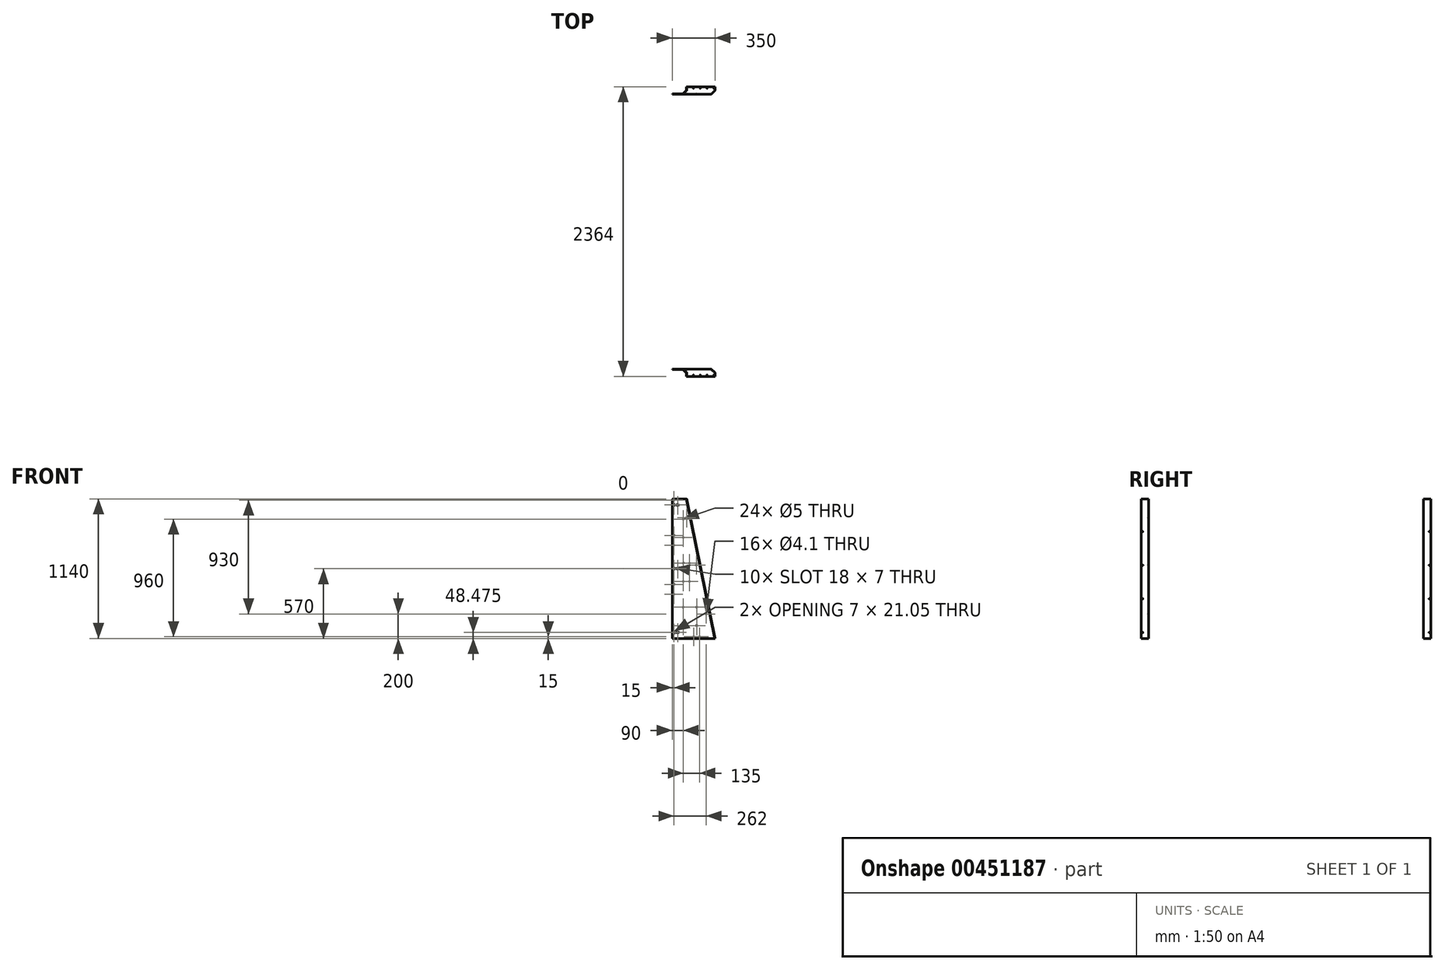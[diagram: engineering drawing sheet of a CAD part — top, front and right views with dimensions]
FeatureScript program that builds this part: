
annotation { "Feature Type Name" : "Feature", "Feature Type Description" : "" }
export const myFeature = defineFeature(function(context is Context, id is Id, definition is map)
    precondition{}
    {
        {
            var Q0;
            Q0=qCreatedBy(makeId("Front.planeOp"),FACE);
            var sketch = newSketch(context, id + "F0", { "sketchPlane" : qUnion([Q0])});
            skLineSegment(sketch, "E0", {"start": v(0, 0) * mm, "end": v(0, 1140) * mm});
            skLineSegment(sketch, "E1", {"start": v(0, 1140) * mm, "end": v(120, 1140) * mm});
            skLineSegment(sketch, "E2", {"start": v(120, 1140) * mm, "end": v(350, 0) * mm});
            skLineSegment(sketch, "E3", {"start": v(350, 0) * mm, "end": v(0, 0) * mm});
            skSolve(sketch);
        }
        {
            var Q0;
            Q0 = qSketchRegion(id + "F0", true);
            extrude(context, id + "F1", {"entities" : qUnion([Q0]), "oppositeDirection" : true, "depth" : 60 * mm, "offsetDistance" : 25 * mm});
        }
        {
            var Q0;
            Q0=makeQuery(id+"F1.opExtrude","SWEPT_FACE",FACE,{"disambiguationData":[OSD([sQuery(id+"F0.wireOp",EDGE,"E1")])]});
            var Q1;
            Q1=makeQuery(id+"F1.opExtrude","SWEPT_FACE",FACE,{"disambiguationData":[OSD([sQuery(id+"F0.wireOp",EDGE,"E0")])]});
            var Q2;
            Q2=makeQuery(id+"F1.opExtrude","CAP_FACE",FACE,{"disambiguationData":[OSD([sQuery(id+"F0.wireOp",EDGE,"E0"),sQuery(id+"F0.wireOp",EDGE,"E1"),sQuery(id+"F0.wireOp",EDGE,"E2"),sQuery(id+"F0.wireOp",EDGE,"E3")])],"isStart":false});
            var Q3;
            Q3=makeQuery(id+"F1.opExtrude","SWEPT_FACE",FACE,{"disambiguationData":[OSD([sQuery(id+"F0.wireOp",EDGE,"E3")])]});
            shell(context, id + "F2", {"entities" : qUnion([Q0, Q1, Q2, Q3]), "thickness" : 3 * mm});
        }
        {
            var Q0;
            Q0=makeQuery(id+"F1.opExtrude","CAP_EDGE",EDGE,{"disambiguationData":[OSD([sQuery(id+"F0.wireOp",EDGE,"E2")])],"isStart":true});
            var Q1;
            {var subQ0=sQuery(id+"F0.wireOp",EDGE,"E2");Q1=makeQuery(id+"F2.opShell","OFFSET_EDGE",EDGE,{"disambiguationData":[OSD([subQ0]),TDD([makeQuery(id+"F1.opExtrude","CAP_EDGE",EDGE,{"disambiguationData":[OSD([subQ0])],"isStart":true})])]});}
            chamfer(context, id + "F3", {"entities" : qUnion([Q0, Q1]), "width" : 30 * mm, "tangentPropagation" : true});
        }
        {
            var Q0;
            {var subQ0=sQuery(id+"F0.wireOp",EDGE,"E2");Q0=makeQuery(id+"F3.opChamfer","BLEND_EDGE",EDGE,{"blendedFrom":[makeQuery(id+"F1.opExtrude","CAP_EDGE",EDGE,{"disambiguationData":[OSD([subQ0])],"isStart":true}),makeQuery(id+"F1.opExtrude","CAP_FACE",FACE,{"disambiguationData":[OSD([sQuery(id+"F0.wireOp",EDGE,"E0"),sQuery(id+"F0.wireOp",EDGE,"E1"),subQ0,sQuery(id+"F0.wireOp",EDGE,"E3")])],"isStart":true})],"blendedInto":[makeQuery(id+"F1.opExtrude","CAP_FACE",FACE,{"disambiguationData":[OSD([sQuery(id+"F0.wireOp",EDGE,"E0"),sQuery(id+"F0.wireOp",EDGE,"E1"),subQ0,sQuery(id+"F0.wireOp",EDGE,"E3")])],"isStart":true})]});}
            var Q1;
            {var subQ0=sQuery(id+"F0.wireOp",EDGE,"E2");Q1=makeQuery(id+"F3.opChamfer","BLEND_EDGE",EDGE,{"blendedFrom":[makeQuery(id+"F2.opShell","OFFSET_EDGE",EDGE,{"disambiguationData":[OSD([subQ0]),TDD([makeQuery(id+"F1.opExtrude","CAP_EDGE",EDGE,{"disambiguationData":[OSD([subQ0])],"isStart":true})])]}),makeQuery(id+"F2.opShell","OFFSET_FACE",FACE,{"disambiguationData":[OSD([sQuery(id+"F0.wireOp",EDGE,"E0"),sQuery(id+"F0.wireOp",EDGE,"E1"),subQ0,sQuery(id+"F0.wireOp",EDGE,"E3")])]})],"blendedInto":[makeQuery(id+"F2.opShell","OFFSET_FACE",FACE,{"disambiguationData":[OSD([sQuery(id+"F0.wireOp",EDGE,"E0"),sQuery(id+"F0.wireOp",EDGE,"E1"),subQ0,sQuery(id+"F0.wireOp",EDGE,"E3")])]})]});}
            var Q2;
            {var subQ0=sQuery(id+"F0.wireOp",EDGE,"E2");Q2=makeQuery(id+"F3.opChamfer","BLEND_EDGE",EDGE,{"blendedFrom":[makeQuery(id+"F1.opExtrude","CAP_EDGE",EDGE,{"disambiguationData":[OSD([subQ0])],"isStart":true}),makeQuery(id+"F1.opExtrude","SWEPT_FACE",FACE,{"disambiguationData":[OSD([subQ0])]})],"blendedInto":[makeQuery(id+"F1.opExtrude","SWEPT_FACE",FACE,{"disambiguationData":[OSD([subQ0])]})]});}
            var Q3;
            {var subQ0=sQuery(id+"F0.wireOp",EDGE,"E2");Q3=makeQuery(id+"F3.opChamfer","BLEND_EDGE",EDGE,{"blendedFrom":[makeQuery(id+"F2.opShell","OFFSET_EDGE",EDGE,{"disambiguationData":[OSD([subQ0]),TDD([makeQuery(id+"F1.opExtrude","CAP_EDGE",EDGE,{"disambiguationData":[OSD([subQ0])],"isStart":true})])]}),makeQuery(id+"F2.opShell","OFFSET_FACE",FACE,{"disambiguationData":[OSD([subQ0])]})],"blendedInto":[makeQuery(id+"F2.opShell","OFFSET_FACE",FACE,{"disambiguationData":[OSD([subQ0])]})]});}
            fillet(context, id + "F4", {"entities" : qUnion([Q0, Q1, Q2, Q3]), "radius" : 10 * mm, "tangentPropagation" : true, "allowEdgeOverflow" : false});
        }
        {
            var Q0;
            Q0=makeQuery(id+"F1.opExtrude","SWEPT_FACE",FACE,{"disambiguationData":[OSD([sQuery(id+"F0.wireOp",EDGE,"E2")])]});
            var sketch = newSketch(context, id + "F5", { "sketchPlane" : qUnion([Q0])});
            skPoint(sketch, "E4", {"position": v(48, -19.22) * mm});
            skPoint(sketch, "E5.0.1.0", {"position": v(48, 260.78) * mm});
            skPoint(sketch, "E5.0.2.0", {"position": v(48, 540.78) * mm});
            skPoint(sketch, "E5.0.3.0", {"position": v(48, 820.78) * mm});
            skPoint(sketch, "E5.0.4.0", {"position": v(48, 1100.78) * mm});
            skLineSegment(sketch, "E5.direction1", {"start": v(48, -19.22) * mm, "end": v(73, -19.22) * mm, "construction": true});
            skLineSegment(sketch, "E5.direction2", {"start": v(48, -19.22) * mm, "end": v(48, 260.78) * mm, "construction": true});
            skSolve(sketch);
        }
        {
            var Q0;
            Q0=makeQuery(id+"F1.opExtrude","CAP_FACE",FACE,{"disambiguationData":[OSD([sQuery(id+"F0.wireOp",EDGE,"E0"),sQuery(id+"F0.wireOp",EDGE,"E1"),sQuery(id+"F0.wireOp",EDGE,"E2"),sQuery(id+"F0.wireOp",EDGE,"E3")])],"isStart":true});
            var sketch = newSketch(context, id + "F6", { "sketchPlane" : qUnion([Q0])});
            skCircle(sketch, "E6", {"center": v(90, 105) * mm, "radius": 2.5 * mm});
            skCircle(sketch, "E7", {"center": v(200, 105) * mm, "radius": 2.5 * mm});
            skCircle(sketch, "E8", {"center": v(200, 255) * mm, "radius": 2.5 * mm});
            skCircle(sketch, "E9", {"center": v(90, 255) * mm, "radius": 2.5 * mm});
            skCircle(sketch, "E10", {"center": v(90, 465) * mm, "radius": 2.5 * mm});
            skCircle(sketch, "E11", {"center": v(90, 615) * mm, "radius": 2.5 * mm});
            skCircle(sketch, "E12", {"center": v(140, 465) * mm, "radius": 2.5 * mm});
            skCircle(sketch, "E13", {"center": v(140, 615) * mm, "radius": 2.5 * mm});
            skCircle(sketch, "E14", {"center": v(90, 825) * mm, "radius": 2.5 * mm});
            skCircle(sketch, "E15", {"center": v(90, 975) * mm, "radius": 2.5 * mm});
            skCircle(sketch, "E16", {"center": v(225, 15) * mm, "radius": 2.5 * mm});
            skCircle(sketch, "E17", {"center": v(175, 15) * mm, "radius": 2.5 * mm});
            skSolve(sketch);
        }
        {
            var Q0;
            Q0 = qSketchRegion(id + "F6", true);
            extrude(context, id + "F7", {"entities" : qUnion([Q0]), "operationType" : NewBodyOperationType.REMOVE, "oppositeDirection" : true, "depth" : 25 * mm, "offsetDistance" : 25 * mm});
        }
        {
            var Q0;
            Q0=sQuery(id+"F5.wireOp",VERTEX,"E4");
            var Q1;
            Q1=sQuery(id+"F5.wireOp",VERTEX,"E5.direction2.end");
            var Q2;
            Q2=sQuery(id+"F5.wireOp",VERTEX,"E5.0.2.0");
            var Q3;
            Q3=sQuery(id+"F5.wireOp",VERTEX,"E5.0.3.0");
            var Q4;
            Q4=sQuery(id+"F5.wireOp",VERTEX,"E5.0.4.0");
            var Q5;
            Q5=makeQuery(id+"F1.opExtrude","SWEPT_BODY",BODY,{"disambiguationData":[OSD([sQuery(id+"F0.wireOp",EDGE,"E0"),sQuery(id+"F0.wireOp",EDGE,"E1"),sQuery(id+"F0.wireOp",EDGE,"E2"),sQuery(id+"F0.wireOp",EDGE,"E3")])]});
            hole(context, id + "F8", {"style" : HoleStyle.SIMPLE, "endStyle" : HoleEndStyle.BLIND, "holeDiameter" : 4.1 * mm, "majorDiameter" : 5 * mm, "holeDepth" : 5 * mm, "tappedDepth" : 12 * mm, "tapClearance" : 3, "locations" : qUnion([Q0, Q1, Q2, Q3, Q4]), "scope" : qUnion([Q5])});
        }
        {
            var Q0;
            Q0=makeQuery(id+"F1.opExtrude","CAP_FACE",FACE,{"disambiguationData":[OSD([sQuery(id+"F0.wireOp",EDGE,"E0"),sQuery(id+"F0.wireOp",EDGE,"E1"),sQuery(id+"F0.wireOp",EDGE,"E2"),sQuery(id+"F0.wireOp",EDGE,"E3")])],"isStart":true});
            var sketch = newSketch(context, id + "F9", { "sketchPlane" : qUnion([Q0])});
            skLineSegment(sketch, "E18.bottom", {"start": v(18.5, 44.5) * mm, "end": v(11.5, 44.5) * mm, "construction": true});
            skLineSegment(sketch, "E18.top", {"start": v(18.5, 55.5) * mm, "end": v(11.5, 55.5) * mm, "construction": true});
            skLineSegment(sketch, "E18.left", {"start": v(18.5, 44.5) * mm, "end": v(18.5, 55.5) * mm});
            skLineSegment(sketch, "E18.right", {"start": v(11.5, 44.5) * mm, "end": v(11.5, 55.5) * mm});
            skPoint(sketch, "E18.middle", {"position": v(15, 50) * mm});
            skArc(sketch, "E19", {"start": v(18.5, 55.5) * mm, "mid": v(15, 59) * mm, "end": v(11.5, 55.5) * mm});
            skArc(sketch, "E20", {"start": v(11.5, 44.5) * mm, "mid": v(15, 41) * mm, "end": v(18.5, 44.5) * mm});
            skLineSegment(sketch, "E21", {"start": v(30, 91.9) * mm, "end": v(30, -40.7) * mm, "construction": true});
            skPoint(sketch, "E22.MirrorP", {"position": v(45, 50) * mm});
            skArc(sketch, "E23.MirrorCS", {"start": v(48.5, 44.5) * mm, "mid": v(45, 41) * mm, "end": v(41.5, 44.5) * mm});
            skLineSegment(sketch, "E24.MirrorCS", {"start": v(41.5, 44.5) * mm, "end": v(48.5, 44.5) * mm, "construction": true});
            skLineSegment(sketch, "E25.MirrorCS", {"start": v(41.5, 55.5) * mm, "end": v(48.5, 55.5) * mm, "construction": true});
            skLineSegment(sketch, "E26.MirrorCS", {"start": v(41.5, 44.5) * mm, "end": v(41.5, 55.5) * mm});
            skLineSegment(sketch, "E27.MirrorCS", {"start": v(48.5, 44.5) * mm, "end": v(48.5, 55.5) * mm});
            skArc(sketch, "E28.MirrorCS", {"start": v(41.5, 55.5) * mm, "mid": v(45, 59) * mm, "end": v(48.5, 55.5) * mm});
            skArc(sketch, "E29.0.1.0", {"start": v(41.5, 575.5) * mm, "mid": v(45, 579) * mm, "end": v(48.5, 575.5) * mm});
            skArc(sketch, "E29.0.1.1", {"start": v(11.5, 564.5) * mm, "mid": v(15, 561) * mm, "end": v(18.5, 564.5) * mm});
            skPoint(sketch, "E29.0.1.2", {"position": v(15, 570) * mm});
            skPoint(sketch, "E29.0.1.3", {"position": v(45, 570) * mm});
            skArc(sketch, "E29.0.1.4", {"start": v(48.5, 564.5) * mm, "mid": v(45, 561) * mm, "end": v(41.5, 564.5) * mm});
            skArc(sketch, "E29.0.1.5", {"start": v(18.5, 575.5) * mm, "mid": v(15, 579) * mm, "end": v(11.5, 575.5) * mm});
            skLineSegment(sketch, "E29.0.1.6", {"start": v(11.5, 564.5) * mm, "end": v(11.5, 575.5) * mm});
            skLineSegment(sketch, "E29.0.1.7", {"start": v(48.5, 564.5) * mm, "end": v(48.5, 575.5) * mm});
            skLineSegment(sketch, "E29.0.1.8", {"start": v(18.5, 564.5) * mm, "end": v(18.5, 575.5) * mm});
            skLineSegment(sketch, "E29.0.1.9", {"start": v(41.5, 564.5) * mm, "end": v(41.5, 575.5) * mm});
            skLineSegment(sketch, "E29.0.1.10", {"start": v(18.5, 564.5) * mm, "end": v(11.5, 564.5) * mm, "construction": true});
            skLineSegment(sketch, "E29.0.1.11", {"start": v(41.5, 575.5) * mm, "end": v(48.5, 575.5) * mm, "construction": true});
            skLineSegment(sketch, "E29.0.1.12", {"start": v(41.5, 564.5) * mm, "end": v(48.5, 564.5) * mm, "construction": true});
            skLineSegment(sketch, "E29.0.1.13", {"start": v(18.5, 575.5) * mm, "end": v(11.5, 575.5) * mm, "construction": true});
            skArc(sketch, "E29.0.2.0", {"start": v(41.5, 1095.5) * mm, "mid": v(45, 1099) * mm, "end": v(48.5, 1095.5) * mm});
            skArc(sketch, "E29.0.2.1", {"start": v(11.5, 1084.5) * mm, "mid": v(15, 1081) * mm, "end": v(18.5, 1084.5) * mm});
            skPoint(sketch, "E29.0.2.2", {"position": v(15, 1090) * mm});
            skPoint(sketch, "E29.0.2.3", {"position": v(45, 1090) * mm});
            skArc(sketch, "E29.0.2.4", {"start": v(48.5, 1084.5) * mm, "mid": v(45, 1081) * mm, "end": v(41.5, 1084.5) * mm});
            skArc(sketch, "E29.0.2.5", {"start": v(18.5, 1095.5) * mm, "mid": v(15, 1099) * mm, "end": v(11.5, 1095.5) * mm});
            skLineSegment(sketch, "E29.0.2.6", {"start": v(11.5, 1084.5) * mm, "end": v(11.5, 1095.5) * mm});
            skLineSegment(sketch, "E29.0.2.7", {"start": v(48.5, 1084.5) * mm, "end": v(48.5, 1095.5) * mm});
            skLineSegment(sketch, "E29.0.2.8", {"start": v(18.5, 1084.5) * mm, "end": v(18.5, 1095.5) * mm});
            skLineSegment(sketch, "E29.0.2.9", {"start": v(41.5, 1084.5) * mm, "end": v(41.5, 1095.5) * mm});
            skLineSegment(sketch, "E29.0.2.10", {"start": v(18.5, 1084.5) * mm, "end": v(11.5, 1084.5) * mm, "construction": true});
            skLineSegment(sketch, "E29.0.2.11", {"start": v(41.5, 1095.5) * mm, "end": v(48.5, 1095.5) * mm, "construction": true});
            skLineSegment(sketch, "E29.0.2.12", {"start": v(41.5, 1084.5) * mm, "end": v(48.5, 1084.5) * mm, "construction": true});
            skLineSegment(sketch, "E29.0.2.13", {"start": v(18.5, 1095.5) * mm, "end": v(11.5, 1095.5) * mm, "construction": true});
            skLineSegment(sketch, "E29.direction1", {"start": v(11.5, 44.5) * mm, "end": v(36.5, 44.5) * mm, "construction": true});
            skLineSegment(sketch, "E29.direction2", {"start": v(11.5, 44.5) * mm, "end": v(11.5, 564.5) * mm, "construction": true});
            skSolve(sketch);
        }
        {
            var Q0;
            Q0 = qSketchRegion(id + "F9", true);
            extrude(context, id + "F10", {"entities" : qUnion([Q0]), "operationType" : NewBodyOperationType.REMOVE, "oppositeDirection" : true, "depth" : 25 * mm, "offsetDistance" : 25 * mm});
        }
        {
            var Q0;
            Q0=qCreatedBy(makeId("Front.planeOp"),FACE);
            cPlane(context, id + "F11", {"entities" : qUnion([Q0]), "cplaneType" : CPlaneType.OFFSET, "offset" : 1122 * mm, "width" : 150 * mm, "height" : 150 * mm});
        }
        {
            var Q0;
            Q0=makeQuery(id+"F1.opExtrude","CAP_FACE",FACE,{"disambiguationData":[OSD([sQuery(id+"F0.wireOp",EDGE,"E0"),sQuery(id+"F0.wireOp",EDGE,"E1"),sQuery(id+"F0.wireOp",EDGE,"E2"),sQuery(id+"F0.wireOp",EDGE,"E3")])],"isStart":true});
            var sketch = newSketch(context, id + "F12", { "sketchPlane" : qUnion([Q0])});
            skCircle(sketch, "E30", {"center": v(15, 40) * mm, "radius": 2.05 * mm});
            skCircle(sketch, "E31", {"center": v(277, 200) * mm, "radius": 2.05 * mm});
            skCircle(sketch, "E32", {"center": v(15, 360) * mm, "radius": 2.05 * mm});
            skCircle(sketch, "E33", {"center": v(15, 440) * mm, "radius": 2.05 * mm});
            skCircle(sketch, "E34", {"center": v(15, 760) * mm, "radius": 2.05 * mm});
            skCircle(sketch, "E35", {"center": v(15, 840) * mm, "radius": 2.05 * mm});
            skCircle(sketch, "E36", {"center": v(15, 1130) * mm, "radius": 2.05 * mm});
            skCircle(sketch, "E37", {"center": v(197, 600) * mm, "radius": 2.05 * mm});
            skCircle(sketch, "E38", {"center": v(119, 985) * mm, "radius": 2.05 * mm});
            skSolve(sketch);
        }
        {
            var Q0;
            Q0 = qSketchRegion(id + "F12", true);
            extrude(context, id + "F13", {"entities" : qUnion([Q0]), "operationType" : NewBodyOperationType.REMOVE, "oppositeDirection" : true, "depth" : 25 * mm, "offsetDistance" : 25 * mm});
        }
        {
            var Q0;
            Q0=makeQuery(id+"F1.opExtrude","SWEPT_BODY",BODY,{"disambiguationData":[OSD([sQuery(id+"F0.wireOp",EDGE,"E0"),sQuery(id+"F0.wireOp",EDGE,"E1"),sQuery(id+"F0.wireOp",EDGE,"E2"),sQuery(id+"F0.wireOp",EDGE,"E3")])]});
            var Q1;
            Q1=qCreatedBy(id+"F11.planeOp",FACE);
            mirror(context, id + "F14", {"entities" : qUnion([Q0]), "mirrorPlane" : qUnion([Q1])});
        }
    });
